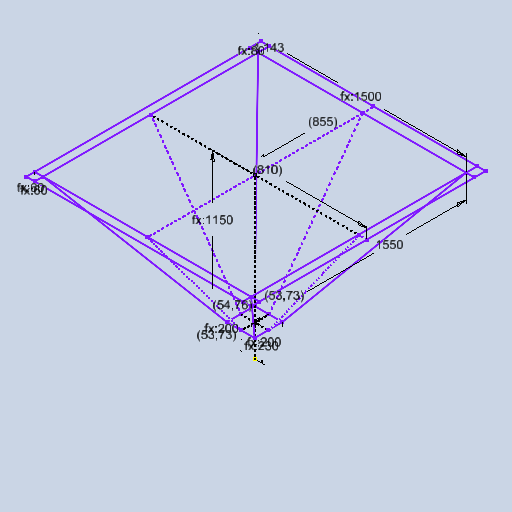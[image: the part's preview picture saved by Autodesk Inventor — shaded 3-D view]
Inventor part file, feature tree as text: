
AUTODESK INVENTOR PART (.ipt)
format: ipt  version: 2025 (Build 290162010, 162A)  size: 124,416 bytes
history: native  units: in
note: dims shown in document units (in); Inventor stores cm internally (conversion verified against a paired STEP export)
features: sketch x2
ambient origin geometry x8: Origin, YZ Plane, XZ Plane, XY Plane, X Axis, Y Axis, Z Axis, Center Point
feature tree (2):
  sketch  "Sketch3"  dims[d16=9.0551in d17=7.874in d18=7.874in d19=45.2756in d20=59.0551in d21=61.0236in d22=0.3692in d23=0.3763in d36=2.3622in d37=2.3622in d38=3.1496in d39=33.6614in d40=0.3692in d41=31.8898in d42=0.1631in]
  sketch  "3D Sketch3"
